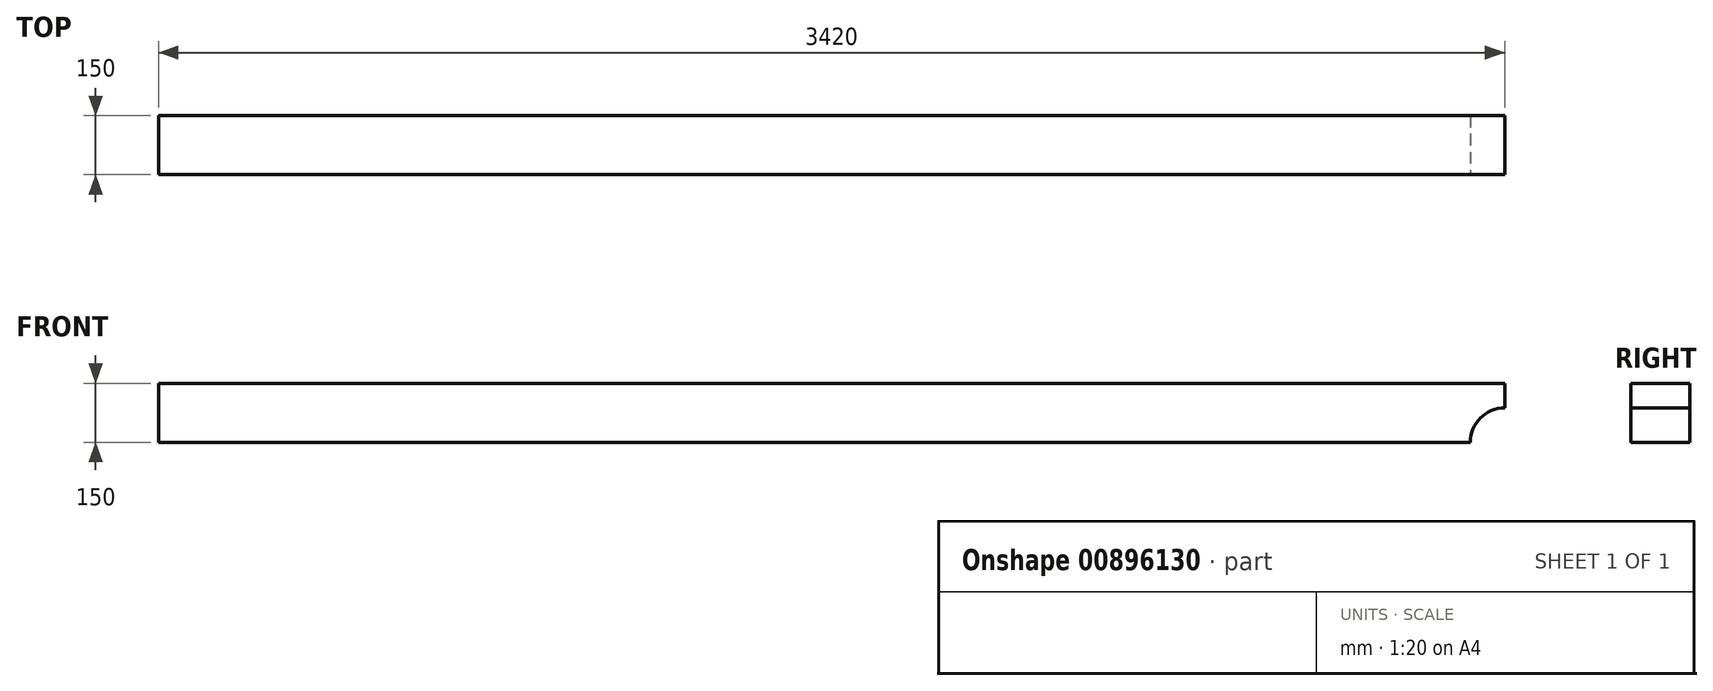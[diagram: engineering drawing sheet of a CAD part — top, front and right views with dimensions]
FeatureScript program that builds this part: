
annotation { "Feature Type Name" : "Feature", "Feature Type Description" : "" }
export const myFeature = defineFeature(function(context is Context, id is Id, definition is map)
    precondition{}
    {
        {
            var Q0;
            Q0=qCreatedBy(makeId("Front.planeOp"),FACE);
            var sketch = newSketch(context, id + "F0", { "sketchPlane" : qUnion([Q0])});
            skLineSegment(sketch, "E0.bottom", {"start": v(0, 0) * mm, "end": v(-3420, 0) * mm});
            skLineSegment(sketch, "E0.top", {"start": v(0, 150) * mm, "end": v(-3420, 150) * mm});
            skLineSegment(sketch, "E0.left", {"start": v(0, 0) * mm, "end": v(0, 150) * mm});
            skLineSegment(sketch, "E0.right", {"start": v(-3420, 0) * mm, "end": v(-3420, 150) * mm});
            skSolve(sketch);
        }
        {
            var Q0;
            Q0=makeQuery(id+"F0.imprint","IMPRINT",FACE,{"disambiguationData":[TD([[makeQuery(id+"F0.imprint","IMPRINT",EDGE,{"derivedFrom":sQuery(id+"F0.wireOp",EDGE,"E0.bottom")}),-1.0]])]});
            extrude(context, id + "F1", {"entities" : qUnion([Q0]), "oppositeDirection" : true, "depth" : 150 * mm, "offsetDistance" : 25 * mm});
        }
        {
            var Q0;
            Q0=sQuery(id+"F0.wireOp",VERTEX,"E0.bottom.start");
            var Q1;
            Q1=makeQuery(id+"F1.opExtrude","SWEPT_BODY",BODY,{"disambiguationData":[OSD([sQuery(id+"F0.wireOp",EDGE,"E0.bottom"),sQuery(id+"F0.wireOp",EDGE,"E0.top"),sQuery(id+"F0.wireOp",EDGE,"E0.left"),sQuery(id+"F0.wireOp",EDGE,"E0.right")])]});
            hole(context, id + "F2", {"style" : HoleStyle.SIMPLE, "endStyle" : HoleEndStyle.THROUGH, "holeDiameter" : 175 * mm, "majorDiameter" : 5 * mm, "isTappedThrough" : true, "tappedDepth" : 12 * mm, "tapClearance" : 3, "locations" : qUnion([Q0]), "scope" : qUnion([Q1])});
        }
    });
